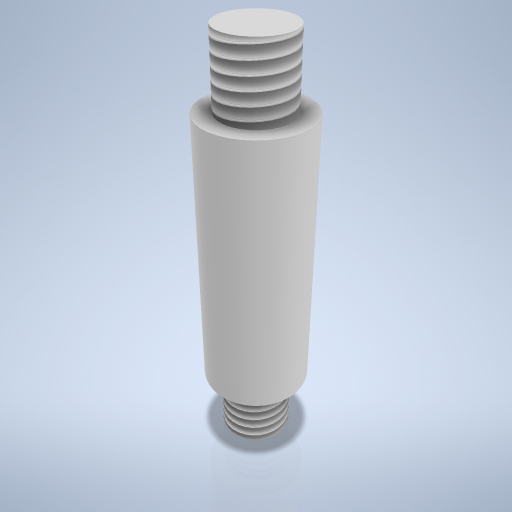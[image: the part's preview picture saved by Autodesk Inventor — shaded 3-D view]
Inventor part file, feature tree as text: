
AUTODESK INVENTOR PART (.ipt)
format: ipt  version: 2024.2 (Build 282272000, 272)  size: 268,288 bytes
history: native  units: mm
features: thread x2, revolve x1, sketch x1
ambient origin geometry x8: Origin, YZ Plane, XZ Plane, XY Plane, X Axis, Y Axis, Z Axis, Center Point
bodies: Volumenkörper1 (feature_tree)
feature tree (4):
  revolve  "Umdrehung1"
  thread  "Gewinde1"  [1 undecoded]
  thread  "Gewinde2"  [1 undecoded]
  sketch  "Skizze1"  dims[d2=24.0mm d3=9.0mm d4=6.0mm d5=90.0deg d6=18.0mm d7=0.0mm d8=18.0mm d9=0.0mm]
note: 2 required parameter values undecoded (feature->parameter linkage not recoverable at this tier; creation-order binding heuristic only, values carry confidence <= 0.55)
